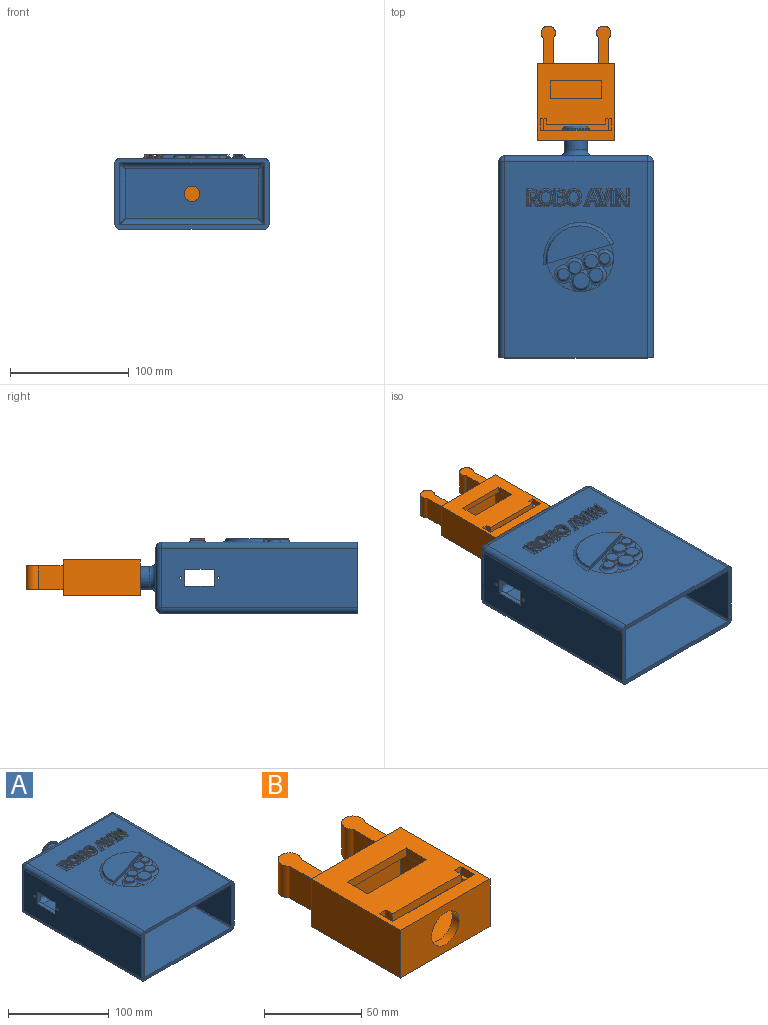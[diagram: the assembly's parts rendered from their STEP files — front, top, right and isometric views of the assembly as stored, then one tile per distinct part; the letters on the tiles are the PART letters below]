
ASSEMBLY  parts=2 mates=1
PART A: 289 faces, bbox 130.2x195.2x65.3 mm
  f0: cylinder r=6.5mm len=29mm, axis (0,-1,0), area 1144.2mm2, adj f1,f21,f22,f283,f284,f285,f286,f287
  f1: plane 18.89x8.5mm, normal (0,1,0), area 69.4mm2, adj f0,f4,f285,f288
  f2: cylinder r=11.5mm len=22.91mm, axis (0,1,0), area 34.1mm2, adj f3,f4,f285,f288
  f3: plane 22.91x10.5mm, normal (0,-1,0), area 62mm2, adj f2,f5,f285,f288
  f4: cone r=9.5mm half-angle=45deg, axis (0,-1,0), area 87.6mm2, adj f1,f2,f285,f288
  f5: cylinder r=9.5mm len=19mm, axis (0,-1,0), area 986.7mm2, adj f3,f59,f281,f283,f284,f285,f286,f287
  f6: plane 2.17x1.68mm, normal (0,0,1), area 1mm2, adj f274,f276,f277,f278
  f7: plane 18.13x9.48mm, normal (0,0,1), area 45.3mm2, adj f192,f273,f274
  f8: plane 13.06x6.59mm, normal (0,0,1), area 20.2mm2, adj f192,f274,f277
  f9: plane 0.13x0.05mm, normal (0,0,1), area 0mm2, adj f231,f234,f235
  f10: plane 3.32x1.5mm, normal (0,0,1), area 1.3mm2, adj f214,f215,f217
  f11: plane 165x120mm, normal (0,0,1), area 16089.2mm2, adj f14,f19,f20,f50,f60,f174,f179,f180
  f12: plane 120x50mm, normal (0,1,0), area 5339.5mm2, adj f43,f46,f47,f50,f59
  f13: plane 165x50mm, normal (-1,0,0), area 7892.4mm2, adj f14,f17,f19,f37,f38,f39,f40,f41
  f14: plane 130x60mm, normal (0,-1,0), area 1435.4mm2, adj f11,f13,f15,f16,f17,f18,f19,f20
  f15: plane 165x50mm, normal (1,0,0), area 7892.4mm2, adj f14,f18,f20,f31,f32,f33,f34,f35
  f16: plane 165x120mm, normal (0,0,-1), area 19800mm2, adj f14,f17,f18,f43
  f17: cylinder r=5mm len=165mm, axis (0,-1,0), area 1295.9mm2, adj f13,f14,f16,f44
  f18: cylinder r=5mm len=165mm, axis (0,1,0), area 1295.9mm2, adj f14,f15,f16,f45
  f19: cylinder r=5mm len=165mm, axis (0,1,0), area 1295.9mm2, adj f11,f13,f14,f48
  f20: cylinder r=5mm len=165mm, axis (0,-1,0), area 1295.9mm2, adj f11,f14,f15,f49
  f21: plane 18.89x8.5mm, normal (0,1,0), area 69.4mm2, adj f0,f282,f284,f287
  f22: plane 112x42mm, normal (0,-1,0), area 4571.3mm2, adj f0,f51,f54,f55,f58
  f23: plane 161x50mm, normal (1,0,0), area 7692.4mm2, adj f14,f27,f29,f37,f38,f39,f40,f41
  f24: plane 161x50mm, normal (-1,0,0), area 7692.4mm2, adj f14,f28,f30,f31,f32,f33,f34,f35
  f25: plane 161x120mm, normal (0,0,-1), area 19320mm2, adj f14,f29,f30,f51
  f26: plane 161x120mm, normal (0,0,1), area 19320mm2, adj f14,f27,f28,f58
  f27: cylinder r=1mm len=161mm, axis (0,-1,0), area 252.9mm2, adj f14,f23,f26,f56
  f28: cylinder r=1mm len=161mm, axis (0,1,0), area 252.9mm2, adj f14,f24,f26,f57
  f29: cylinder r=1mm len=161mm, axis (0,1,0), area 252.9mm2, adj f14,f23,f25,f52
  f30: cylinder r=1mm len=161mm, axis (0,-1,0), area 252.9mm2, adj f14,f24,f25,f53
  f31: plane 25x4mm, normal (0,0,1), area 100mm2, adj f15,f24,f32,f34
  f32: plane 14x4mm, normal (0,-1,0), area 56mm2, adj f15,f24,f31,f33
  f33: plane 25x4mm, normal (0,0,-1), area 100mm2, adj f15,f24,f32,f34
  f34: plane 14x4mm, normal (0,1,0), area 56mm2, adj f15,f24,f31,f33
  f35: cylinder r=1.1mm len=4mm, axis (-1,0,0), area 27.6mm2, adj f15,f24
  f36: cylinder r=1.1mm len=4mm, axis (-1,0,0), area 27.6mm2, adj f15,f24
  f37: plane 14x4mm, normal (0,1,0), area 56mm2, adj f13,f23,f38,f40
  f38: plane 25x4mm, normal (0,0,-1), area 100mm2, adj f13,f23,f37,f39
  f39: plane 14x4mm, normal (0,-1,0), area 56mm2, adj f13,f23,f38,f40
  f40: plane 25x4mm, normal (0,0,1), area 100mm2, adj f13,f23,f37,f39
  f41: cylinder r=1.1mm len=4mm, axis (-1,0,0), area 27.6mm2, adj f13,f23
  f42: cylinder r=1.1mm len=4mm, axis (-1,0,0), area 27.6mm2, adj f13,f23
  f43: cylinder r=5mm len=120mm, axis (-1,0,0), area 942.5mm2, adj f12,f16,f44,f45
  f44: sphere r=5mm, area 39.3mm2, adj f17,f43,f46
  f45: sphere r=5mm, area 53.5mm2, adj f18,f43,f47
  f46: cylinder r=5mm len=50mm, axis (0,0,1), area 392.7mm2, adj f12,f13,f44,f48
  f47: cylinder r=5mm len=50mm, axis (0,0,-1), area 392.7mm2, adj f12,f15,f45,f49
  f48: sphere r=5mm, area 39.3mm2, adj f19,f46,f50
  f49: sphere r=5mm, area 25mm2, adj f20,f47,f50
  f50: cylinder r=5mm len=120mm, axis (1,0,0), area 942.5mm2, adj f11,f12,f48,f49
  f51: cylinder r=5mm len=120mm, axis (-1,0,0), area 911.1mm2, adj f22,f25,f52,f53
  f52: bspline ~5.78x5mm, area 5.4mm2, adj f29,f51,f54
  f53: bspline ~5.78x5mm, area 5.4mm2, adj f30,f51,f55
  f54: cylinder r=5mm len=50mm, axis (0,0,-1), area 361.3mm2, adj f22,f23,f52,f56
  f55: cylinder r=5mm len=50mm, axis (0,0,1), area 361.3mm2, adj f22,f24,f53,f57
  f56: bspline ~5.78x5mm, area 5.4mm2, adj f27,f54,f58
  f57: bspline ~5.78x5mm, area 5.4mm2, adj f28,f55,f58
  f58: cylinder r=5mm len=120mm, axis (1,0,0), area 911.1mm2, adj f22,f26,f56,f57
  f59: torus R=14.5mm, axis (0,1,0), area 558.5mm2, adj f5,f12
  f60: plane 59.16x17.8mm, normal (0.29,-0.96,0), area 225.9mm2, adj f11,f61,f192,f193,f279
  f61: plane 53.39x31.67mm, normal (0,0,1), area 985.1mm2, adj f60,f279
  f62: plane 3x1.85mm, normal (0,1,0), area 5.6mm2, adj f63,f79,f80,f81
  f63: plane 4.44x3mm, normal (1,0,0), area 13.3mm2, adj f62,f64,f80,f81
  f64: plane 3x1.76mm, normal (0,-1,0), area 5.3mm2, adj f63,f65,f80,f81
  f65: extruded ~3x2.18mm, area 6.8mm2, adj f64,f66,f80,f81
  f66: extruded ~3x1.66mm, area 5.6mm2, adj f65,f67,f80,f81
  f67: extruded ~3x1.71mm, area 5.7mm2, adj f66,f79,f80,f81
  f68: plane 4.83x1.5mm, normal (1,0,0), area 7.2mm2, adj f69,f78,f80,f206
  f69: plane 2.43x1.5mm, normal (0,-1,0), area 3.6mm2, adj f68,f70,f80,f208
  f70: plane 4.83x2.81mm, normal (-0.86,-0.5,0), area 8.4mm2, adj f69,f71,f80,f210
  f71: plane 1.6x1.5mm, normal (0,-1,0), area 2.4mm2, adj f70,f72,f80,f212
  f72: plane 5.22x3.16mm, normal (0.86,0.52,0), area 9.1mm2, adj f71,f73,f80,f214
  f73: extruded ~3.12x2.34mm, area 6.3mm2, adj f72,f74,f80,f215
  f74: extruded ~2.46x1.5mm, area 4.1mm2, adj f73,f75,f80,f216
  f75: extruded ~3.16x1.5mm, area 5mm2, adj f74,f76,f80,f213
  f76: plane 3.19x1.5mm, normal (0,1,0), area 4.8mm2, adj f75,f77,f80,f211
  f77: plane 11.62x1.5mm, normal (-1,0,0), area 17.4mm2, adj f76,f78,f80,f209
  f78: plane 1.5x1.35mm, normal (0,-1,0), area 2mm2, adj f68,f77,f80,f207
  f79: extruded ~3x2.1mm, area 6.6mm2, adj f62,f67,f80,f81
  f80: plane 11.62x8.19mm, normal (0,0,1), area 40.5mm2, adj f62,f63,f64,f65,f66,f67,f68,f69
  f81: plane 4.62x4.44mm, normal (0,0,1), area 18.5mm2, adj f62,f63,f64,f65,f66,f67,f79
  f82: extruded ~3.58x3mm, area 11.4mm2, adj f83,f97,f98,f99
  f83: extruded ~3.55x3mm, area 11.3mm2, adj f82,f84,f98,f99
  f84: extruded ~3x2.94mm, area 9.9mm2, adj f83,f85,f98,f99
  f85: extruded ~3x2.9mm, area 9.8mm2, adj f84,f86,f98,f99
  f86: extruded ~3.56x3mm, area 11.3mm2, adj f85,f87,f98,f99
  f87: extruded ~3.59x3mm, area 11.4mm2, adj f86,f88,f98,f99
  f88: extruded ~3x2.92mm, area 9.8mm2, adj f87,f97,f98,f99
  f89: extruded ~4.39x1.5mm, area 7.1mm2, adj f90,f96,f98,f223
  f90: extruded ~4.39x1.5mm, area 7.1mm2, adj f89,f91,f98,f224
  f91: extruded ~3.91x1.59mm, area 6.5mm2, adj f90,f92,f98,f222
  f92: extruded ~3.97x1.56mm, area 6.6mm2, adj f91,f93,f98,f220
  f93: extruded ~4.4x1.5mm, area 7.1mm2, adj f92,f94,f98,f218
  f94: extruded ~4.43x1.5mm, area 7.1mm2, adj f93,f95,f98,f217
  f95: extruded ~3.96x1.57mm, area 6.6mm2, adj f94,f96,f98,f219
  f96: extruded ~3.92x1.6mm, area 6.6mm2, adj f89,f95,f98,f221
  f97: extruded ~3x2.92mm, area 9.8mm2, adj f82,f88,f98,f99
  f98: plane 11.96x10.69mm, normal (0,0,1), area 42.7mm2, adj f82,f83,f84,f85,f86,f87,f88,f89
  f99: plane 9.57x7.83mm, normal (0,0,1), area 62.1mm2, adj f82,f83,f84,f85,f86,f87,f88,f97
  f100: plane 4.35x3mm, normal (1,0,0), area 13mm2, adj f101,f124,f125,f126
  f101: plane 3x2.31mm, normal (0,-1,0), area 6.9mm2, adj f100,f102,f125,f126
  f102: extruded ~3x2.21mm, area 6.9mm2, adj f101,f103,f125,f126
  f103: extruded ~3x1.59mm, area 5.5mm2, adj f102,f104,f125,f126
  f104: extruded ~3x1.71mm, area 5.8mm2, adj f103,f105,f125,f126
  f105: extruded ~3x2.12mm, area 6.7mm2, adj f104,f124,f125,f126
  f106: plane 3x2.23mm, normal (0,1,0), area 6.7mm2, adj f107,f122,f125,f127
  f107: plane 3.8x3mm, normal (1,0,0), area 11.4mm2, adj f106,f108,f125,f127
  f108: plane 3x1.99mm, normal (0,-1,0), area 6mm2, adj f107,f109,f125,f127
  f109: extruded ~3x2.23mm, area 6.9mm2, adj f108,f110,f125,f127
  f110: extruded ~3x1.41mm, area 5mm2, adj f109,f111,f125,f127
  f111: extruded ~3x1.51mm, area 5.1mm2, adj f110,f122,f125,f127
  f112: plane 3.28x1.5mm, normal (0,1,0), area 4.9mm2, adj f113,f123,f125,f226
  f113: plane 11.62x1.5mm, normal (-1,0,0), area 17.4mm2, adj f112,f114,f125,f225
  f114: plane 4.05x1.5mm, normal (0,-1,0), area 6.1mm2, adj f113,f115,f125,f227
  f115: extruded ~2.94x1.5mm, area 4.7mm2, adj f114,f116,f125,f229
  f116: extruded ~2.43x1.5mm, area 4.1mm2, adj f115,f117,f125,f233
  f117: extruded ~2.78x2.65mm, area 6.4mm2, adj f116,f118,f125,f234
  f118: plane 1.85x0.09mm, normal (1,0,0), area 0.1mm2, adj f117,f119,f125,f230,f234
  f119: extruded ~1.68x1.5mm, area 2.9mm2, adj f118,f120,f125,f230
  f120: extruded ~1.71x1.5mm, area 2.8mm2, adj f119,f121,f125,f231
  f121: extruded ~2.18x1.5mm, area 3.8mm2, adj f120,f123,f125,f232
  f122: extruded ~3x2.06mm, area 6.4mm2, adj f106,f111,f125,f127
  f123: extruded ~3.35x1.5mm, area 5.2mm2, adj f112,f121,f125,f228
  f124: plane 3x2.43mm, normal (0,1,0), area 7.3mm2, adj f100,f105,f125,f126
  f125: plane 11.62x8.05mm, normal (0,0,1), area 46mm2, adj f100,f101,f102,f103,f104,f105,f106,f107
  f126: plane 5.25x4.35mm, normal (0,0,1), area 20.8mm2, adj f100,f101,f102,f103,f104,f105,f124
  f127: plane 4.91x3.8mm, normal (0,0,1), area 17.1mm2, adj f106,f107,f108,f109,f110,f111,f122
  f128: extruded ~3.58x3mm, area 11.4mm2, adj f129,f143,f144,f145
  f129: extruded ~3.55x3mm, area 11.3mm2, adj f128,f130,f144,f145
  f130: extruded ~3x2.94mm, area 9.9mm2, adj f129,f131,f144,f145
  f131: extruded ~3x2.9mm, area 9.8mm2, adj f130,f132,f144,f145
  f132: extruded ~3.56x3mm, area 11.3mm2, adj f131,f133,f144,f145
  f133: extruded ~3.59x3mm, area 11.4mm2, adj f132,f134,f144,f145
  f134: extruded ~3x2.92mm, area 9.8mm2, adj f133,f143,f144,f145
  f135: extruded ~4.39x1.5mm, area 7.1mm2, adj f136,f142,f144,f242
  f136: extruded ~4.39x1.5mm, area 7.1mm2, adj f135,f137,f144,f240
  f137: extruded ~3.91x1.59mm, area 6.5mm2, adj f136,f138,f144,f238
  f138: extruded ~3.97x1.56mm, area 6.6mm2, adj f137,f139,f144,f236
  f139: extruded ~4.4x1.5mm, area 7.1mm2, adj f138,f140,f144,f235
  f140: extruded ~4.43x1.5mm, area 7.1mm2, adj f139,f141,f144,f237
  f141: extruded ~3.96x1.57mm, area 6.6mm2, adj f140,f142,f144,f239
  f142: extruded ~3.92x1.6mm, area 6.6mm2, adj f135,f141,f144,f241
  f143: extruded ~3x2.92mm, area 9.8mm2, adj f128,f134,f144,f145
  f144: plane 11.96x10.69mm, normal (0,0,1), area 42.7mm2, adj f128,f129,f130,f131,f132,f133,f134,f135
  f145: plane 9.57x7.83mm, normal (0,0,1), area 62.1mm2, adj f128,f129,f130,f131,f132,f133,f134,f143
  f146: plane 3.6x3mm, normal (-0.94,-0.35,0), area 11.5mm2, adj f147,f158,f159,f160
  f147: plane 3.76x3mm, normal (0,1,0), area 11.3mm2, adj f146,f148,f159,f160
  f148: plane 3.6x3mm, normal (0.94,-0.35,0), area 11.6mm2, adj f147,f149,f159,f160
  f149: extruded ~3x1.68mm, area 5.2mm2, adj f148,f158,f159,f160
  f150: plane 3.69x1.5mm, normal (-0.93,-0.36,0), area 6mm2, adj f151,f157,f159,f258
  f151: plane 1.5x1.4mm, normal (0,-1,0), area 2.1mm2, adj f150,f152,f159,f259
  f152: plane 11.67x4.57mm, normal (0.93,0.36,0), area 18.8mm2, adj f151,f153,f159,f257
  f153: plane 1.5x1.14mm, normal (0,1,0), area 1.7mm2, adj f152,f154,f159,f255
  f154: plane 11.67x4.59mm, normal (-0.93,0.37,0), area 18.8mm2, adj f153,f155,f159,f253
  f155: plane 1.5x1.37mm, normal (0,-1,0), area 2.1mm2, adj f154,f156,f159,f252
  f156: plane 3.69x1.5mm, normal (0.93,-0.36,0), area 5.9mm2, adj f155,f157,f159,f254
  f157: plane 4.66x1.5mm, normal (0,-1,0), area 7mm2, adj f150,f156,f159,f256
  f158: extruded ~3x1.68mm, area 5.3mm2, adj f146,f149,f159,f160
  f159: plane 11.67x10.3mm, normal (0,0,1), area 34.7mm2, adj f146,f147,f148,f149,f150,f151,f152,f153
  f160: plane 5.28x3.76mm, normal (0,0,1), area 9.5mm2, adj f146,f147,f148,f149,f158
  f161: plane 1.5x1.45mm, normal (0,1,0), area 2.2mm2, adj f162,f169,f170,f246
  f162: plane 7.47x2.65mm, normal (-0.94,0.33,0), area 11.9mm2, adj f161,f163,f170,f248
  f163: extruded ~2.57x1.5mm, area 4mm2, adj f162,f164,f170,f250
  f164: extruded ~2.52x1.5mm, area 3.9mm2, adj f163,f165,f170,f251
  f165: plane 7.52x2.67mm, normal (0.94,0.33,0), area 12mm2, adj f164,f166,f170,f249
  f166: plane 1.5x1.43mm, normal (0,1,0), area 2.1mm2, adj f165,f167,f170,f247
  f167: plane 11.62x4.17mm, normal (-0.94,-0.34,0), area 18.5mm2, adj f166,f168,f170,f245
  f168: plane 1.5x1.34mm, normal (0,-1,0), area 2mm2, adj f167,f169,f170,f243
  f169: plane 11.62x4.19mm, normal (0.94,-0.34,0), area 18.5mm2, adj f161,f168,f170,f244
  f170: plane 11.62x9.69mm, normal (0,0,1), area 31.3mm2, adj f161,f162,f163,f164,f165,f166,f167,f168
  f171: plane 11.62x1.5mm, normal (-1,0,0), area 17.4mm2, adj f172,f174,f175,f271
  f172: plane 1.5x1.35mm, normal (0,-1,0), area 2mm2, adj f171,f173,f175,f272
  f173: plane 11.62x1.5mm, normal (1,0,0), area 17.4mm2, adj f172,f174,f175,f270
  f174: plane 3.63x3.01mm, normal (0,1,0), area 4.9mm2, adj f11,f171,f173,f175,f244,f270,f271
  f175: plane 11.62x1.35mm, normal (0,0,1), area 15.7mm2, adj f171,f172,f173,f174
  f176: plane 1.54x1.5mm, normal (0,-1,0), area 2.3mm2, adj f177,f190,f191,f265
  f177: plane 11.62x1.5mm, normal (1,0,0), area 17.4mm2, adj f176,f178,f191,f263
  f178: plane 1.5x1.26mm, normal (0,1,0), area 1.9mm2, adj f177,f179,f191,f261
  f179: plane 8.17x3mm, normal (-1,0,0), area 20.5mm2, adj f11,f178,f180,f191,f261
  f180: extruded ~3x1.67mm, area 4.9mm2, adj f11,f179,f181,f191,f260
  f181: extruded ~2.8x1.38mm, area 3.4mm2, adj f180,f182,f191,f260
  f182: plane 1.91x0.08mm, normal (0,1,0), area 0.1mm2, adj f181,f183,f191,f260
  f183: plane 9.71x6.33mm, normal (0.84,0.55,0), area 17.4mm2, adj f182,f184,f191,f260
  f184: plane 1.53x1.5mm, normal (0,1,0), area 2.3mm2, adj f183,f185,f191,f262
  f185: plane 11.62x1.5mm, normal (-1,0,0), area 17.4mm2, adj f184,f186,f191,f264
  f186: plane 1.5x1.25mm, normal (0,-1,0), area 1.9mm2, adj f185,f187,f191,f266
  f187: plane 6.6x1.5mm, normal (1,0,0), area 9.9mm2, adj f186,f188,f191,f268
  f188: extruded ~3.15x1.5mm, area 4.7mm2, adj f187,f189,f191,f269
  f189: plane 1.8x0.07mm, normal (0,-1,0), area 0.1mm2, adj f188,f190,f191,f267,f269
  f190: plane 9.75x6.35mm, normal (-0.84,-0.55,0), area 17.5mm2, adj f176,f189,f191,f267
  f191: plane 11.62x9.08mm, normal (0,0,1), area 44.6mm2, adj f176,f177,f178,f179,f180,f181,f182,f183
  f192: cylinder r=27.99mm len=55.64mm, axis (0,0,1), area 95.4mm2, adj f7,f8,f11,f60,f193,f273,f274,f277
  f193: plane 55.58x39.34mm, normal (0,0,1), area 263.7mm2, adj f60,f192,f273,f275,f276,f277,f278
  f194: plane 13.52x13.52mm, normal (0,0,1), area 143.5mm2, adj f195
  f195: cylinder r=6.76mm len=13.52mm, axis (0,0,-1), area 42.5mm2, adj f194,f277
  f196: plane 8.85x8.85mm, normal (0,0,1), area 61.5mm2, adj f197
  f197: cylinder r=4.42mm len=8.85mm, axis (0,0,-1), area 27.8mm2, adj f196,f273
  f198: plane 11.17x11.17mm, normal (0,0,1), area 98.1mm2, adj f199
  f199: cylinder r=5.59mm len=11.17mm, axis (0,0,-1), area 35.1mm2, adj f198,f276
  f200: plane 10.12x10.12mm, normal (0,0,1), area 80.4mm2, adj f201
  f201: cylinder r=5.06mm len=10.12mm, axis (0,0,-1), area 31.8mm2, adj f200,f278
  f202: plane 9.55x9.55mm, normal (0,0,1), area 71.7mm2, adj f203
  f203: cylinder r=4.78mm len=9.55mm, axis (0,0,-1), area 30mm2, adj f202,f275
  f204: plane 11.31x11.31mm, normal (0,0,1), area 100.4mm2, adj f205
  f205: cylinder r=5.65mm len=11.31mm, axis (0,0,-1), area 35.5mm2, adj f204,f274
  f206: cylinder r=1.5mm len=6.33mm, axis (0,1,0), area 11.4mm2, adj f11,f68,f207,f208
  f207: cylinder r=1.5mm len=4.35mm, axis (1,0,0), area 6.7mm2, adj f11,f78,f206,f209
  f208: cylinder r=1.5mm len=2.43mm, axis (1,0,0), area 3.7mm2, adj f11,f69,f206,f210
  f209: cylinder r=1.5mm len=14.62mm, axis (0,-1,0), area 30.9mm2, adj f11,f77,f207,f211
  f210: cylinder r=1.5mm len=6.33mm, axis (0.5,-0.86,0), area 13.2mm2, adj f11,f70,f208,f212
  f211: cylinder r=1.5mm len=4.69mm, axis (-1,0,0), area 9.3mm2, adj f11,f76,f209,f213
  f212: cylinder r=1.5mm len=5.12mm, axis (1,0,0), area 7.9mm2, adj f11,f71,f210,f214
  f213: bspline ~5.7x2.68mm, area 8.7mm2, adj f11,f75,f211,f216
  f214: cylinder r=1.5mm len=8.27mm, axis (-0.52,0.86,0), area 15.6mm2, adj f10,f11,f72,f212,f215,f217
  f215: bspline ~5.23x4.94mm, area 9.3mm2, adj f10,f73,f214,f216,f217,f218
  f216: bspline ~4.76x3.06mm, area 7.5mm2, adj f11,f74,f213,f215,f218
  f217: bspline ~7.62x3.42mm, area 12.1mm2, adj f10,f11,f94,f214,f215,f218,f219
  f218: bspline ~7.55x3.42mm, area 11.3mm2, adj f11,f93,f215,f216,f217,f220
  f219: bspline ~6.91x3.89mm, area 11.4mm2, adj f11,f95,f217,f221
  f220: bspline ~6.94x3.89mm, area 11.5mm2, adj f11,f92,f218,f222
  f221: bspline ~6.84x3.91mm, area 11.4mm2, adj f11,f96,f219,f223
  f222: bspline ~6.02x3.89mm, area 11.4mm2, adj f11,f91,f220,f224
  f223: bspline ~7.54x3.43mm, area 11.7mm2, adj f11,f89,f221,f224,f225
  f224: bspline ~7.54x3.43mm, area 11.7mm2, adj f11,f90,f222,f223,f225
  f225: cylinder r=1.5mm len=14.62mm, axis (0,-1,0), area 30.3mm2, adj f11,f113,f223,f224,f226,f227
  f226: cylinder r=1.5mm len=4.78mm, axis (-1,0,0), area 9.5mm2, adj f11,f112,f225,f228
  f227: cylinder r=1.5mm len=5.55mm, axis (1,0,0), area 11.3mm2, adj f11,f114,f225,f229
  f228: bspline ~5.62x2.63mm, area 8.9mm2, adj f11,f123,f226,f232
  f229: bspline ~4.68x2.86mm, area 8.3mm2, adj f11,f115,f227,f233
  f230: bspline ~3.37x2.49mm, area 2.5mm2, adj f118,f119,f231,f234
  f231: bspline ~3.66x2.44mm, area 4.8mm2, adj f9,f120,f230,f232,f234,f235
  f232: bspline ~4.47x3.09mm, area 7.2mm2, adj f11,f121,f228,f231,f235
  f233: bspline ~4.27x3.15mm, area 7.3mm2, adj f11,f116,f229,f234,f237
  f234: bspline ~5.46x4.31mm, area 7.7mm2, adj f9,f117,f118,f230,f231,f233,f235,f237
  f235: bspline ~7.55x3.42mm, area 11.6mm2, adj f9,f11,f139,f231,f232,f234,f236,f237
  f236: bspline ~6.94x3.89mm, area 11.5mm2, adj f11,f138,f235,f238
  f237: bspline ~7.62x3.42mm, area 11.1mm2, adj f11,f140,f233,f234,f235,f239
  f238: bspline ~6.02x3.89mm, area 11.4mm2, adj f11,f137,f236,f240
  f239: bspline ~6.91x3.89mm, area 11.4mm2, adj f11,f141,f237,f241
  f240: bspline ~7.54x3.43mm, area 12mm2, adj f11,f136,f238,f242
  f241: bspline ~6.84x3.91mm, area 11.4mm2, adj f11,f142,f239,f242
  f242: bspline ~7.54x3.43mm, area 12mm2, adj f11,f135,f240,f241
  f243: cylinder r=1.5mm len=3.44mm, axis (1,0,0), area 5.6mm2, adj f11,f168,f244,f245
  f244: cylinder r=1.5mm len=15.13mm, axis (0.34,0.94,0), area 30.5mm2, adj f11,f169,f174,f243,f246,f271
  f245: cylinder r=1.5mm len=15.12mm, axis (0.34,-0.94,0), area 32.8mm2, adj f11,f167,f243,f247
  f246: cylinder r=1.5mm len=4.65mm, axis (-1,0,0), area 7.2mm2, adj f11,f161,f244,f248
  f247: cylinder r=1.5mm len=4.62mm, axis (-1,0,0), area 7.1mm2, adj f11,f166,f245,f249
  f248: cylinder r=1.5mm len=8.97mm, axis (-0.33,-0.94,0), area 19.2mm2, adj f11,f162,f246,f249,f250
  f249: cylinder r=1.5mm len=9.02mm, axis (-0.33,0.94,0), area 18.9mm2, adj f11,f165,f247,f248,f250,f251
  f250: bspline ~4.16x2.53mm, area 2.7mm2, adj f163,f248,f249,f251
  f251: bspline ~3.78x2.38mm, area 2.1mm2, adj f164,f249,f250
  f252: cylinder r=1.5mm len=4.6mm, axis (1,0,0), area 7mm2, adj f11,f155,f253,f254
  f253: cylinder r=1.5mm len=15.22mm, axis (-0.37,-0.93,0), area 33.3mm2, adj f11,f154,f252,f255
  f254: cylinder r=1.5mm len=5.19mm, axis (0.36,0.93,0), area 9.3mm2, adj f11,f156,f252,f256
  f255: cylinder r=1.5mm len=3.18mm, axis (-1,0,0), area 5.1mm2, adj f11,f153,f253,f257
  f256: cylinder r=1.5mm len=4.66mm, axis (1,0,0), area 8.6mm2, adj f11,f157,f254,f258
  f257: cylinder r=1.5mm len=15.21mm, axis (-0.36,0.93,0), area 33.3mm2, adj f11,f152,f255,f259
  f258: cylinder r=1.5mm len=5.19mm, axis (0.36,-0.93,0), area 9.3mm2, adj f11,f150,f256,f259
  f259: cylinder r=1.5mm len=4.62mm, axis (1,0,0), area 7.1mm2, adj f11,f151,f257,f258
  f260: cylinder r=1.5mm len=11.24mm, axis (-0.55,0.84,0), area 26.2mm2, adj f11,f180,f181,f182,f183,f262
  f261: cylinder r=1.5mm len=2.76mm, axis (-1,0,0), area 4.7mm2, adj f11,f178,f179,f263
  f262: cylinder r=1.5mm len=3.84mm, axis (-1,0,0), area 6.3mm2, adj f11,f184,f260,f264
  f263: cylinder r=1.5mm len=14.62mm, axis (0,1,0), area 30.9mm2, adj f11,f177,f261,f265
  f264: cylinder r=1.5mm len=14.62mm, axis (0,-1,0), area 30.9mm2, adj f11,f185,f262,f266
  f265: cylinder r=1.5mm len=3.85mm, axis (1,0,0), area 6.4mm2, adj f11,f176,f263,f267
  f266: cylinder r=1.5mm len=4.25mm, axis (1,0,0), area 6.5mm2, adj f11,f186,f264,f268
  f267: cylinder r=1.5mm len=11.26mm, axis (0.55,-0.84,0), area 23.7mm2, adj f11,f189,f190,f265,f268,f269
  f268: cylinder r=1.5mm len=8.1mm, axis (0,1,0), area 16.7mm2, adj f11,f187,f266,f267,f269
  f269: bspline ~4.34x1.69mm, area 3.6mm2, adj f188,f189,f267,f268
  f270: cylinder r=1.5mm len=13.12mm, axis (0,1,0), area 29.1mm2, adj f11,f173,f174,f272
  f271: cylinder r=1.5mm len=13.12mm, axis (0,-1,0), area 27.6mm2, adj f11,f171,f174,f244,f272
  f272: cylinder r=1.5mm len=4.35mm, axis (1,0,0), area 6.7mm2, adj f11,f172,f270,f271
  f273: torus R=7.42mm, axis (0,0,1), area 144mm2, adj f7,f192,f193,f197,f274,f276
  f274: torus R=8.65mm, axis (0,0,1), area 152.1mm2, adj f6,f7,f8,f192,f205,f273,f276,f277
  f275: torus R=7.78mm, axis (0,0,1), area 149.8mm2, adj f193,f203,f277,f278
  f276: torus R=8.59mm, axis (0,0,1), area 151.5mm2, adj f6,f193,f199,f273,f274,f278
  f277: torus R=9.76mm, axis (0,0,1), area 175.3mm2, adj f6,f8,f192,f193,f195,f274,f275,f278
  f278: torus R=8.06mm, axis (0,0,1), area 129.9mm2, adj f6,f193,f201,f275,f276,f277
  f279: torus R=31.12mm, axis (0,0,1), area 389.5mm2, adj f11,f60,f61
  f280: cylinder r=11.5mm len=22.91mm, axis (0,1,0), area 34.1mm2, adj f281,f282,f284,f287
  f281: plane 22.91x10.5mm, normal (0,-1,0), area 62mm2, adj f5,f280,f284,f287
  f282: cone r=9.5mm half-angle=45deg, axis (0,-1,0), area 87.6mm2, adj f21,f280,f284,f287
  f283: plane 3.08x2mm, normal (0,1,0), area 6mm2, adj f0,f5,f284,f285
  f284: plane 10.02x5.05mm, normal (0,0,1), area 34.3mm2, adj f0,f5,f21,f280,f281,f282,f283
  f285: plane 10.02x5.05mm, normal (0,0,-1), area 34.3mm2, adj f0,f1,f2,f3,f4,f5,f283
  f286: plane 3.08x2mm, normal (0,1,0), area 6mm2, adj f0,f5,f287,f288
  f287: plane 10.02x5.05mm, normal (0,0,1), area 34.3mm2, adj f0,f5,f21,f280,f281,f282,f286
  f288: plane 10.02x5.05mm, normal (0,0,-1), area 34.3mm2, adj f0,f1,f2,f3,f4,f5,f286
PART B: 39 faces, bbox 65x96.2x30 mm
  f0: plane 27.5x20mm, normal (0,1,0), area 392.9mm2, adj f31,f33,f34,f38
  f1: plane 9.75x2.16mm, normal (0,0,1), area 21.1mm2, adj f7,f13,f18,f35
  f2: plane 65x30mm, normal (0,1,0), area 1614.5mm2, adj f3,f5,f6,f19,f21,f22,f24,f25
  f3: plane 65x30mm, normal (-1,0,0), area 1950mm2, adj f2,f4,f6,f19
  f4: plane 65x30mm, normal (0,-1,0), area 1635.8mm2, adj f3,f5,f6,f19,f38
  f5: plane 65x30mm, normal (1,0,0), area 1950mm2, adj f2,f4,f6,f19
  f6: plane 65x65mm, normal (0,0,-1), area 4225mm2, adj f2,f3,f4,f5
  f7: plane 59.33x5mm, normal (0,1,0), area 296.6mm2, adj f1,f8,f18,f19,f20,f31
  f8: plane 9.75x5mm, normal (1,0,0), area 48.7mm2, adj f7,f9,f19,f20
  f9: plane 5x4.66mm, normal (0,-1,0), area 23.3mm2, adj f8,f10,f19,f20,f32
  f10: plane 5x4.75mm, normal (-1,0,0), area 23.7mm2, adj f9,f11,f19,f32
  f11: plane 50x5mm, normal (0,-1,0), area 250mm2, adj f10,f12,f19,f32
  f12: plane 5x4.75mm, normal (1,0,0), area 23.7mm2, adj f11,f13,f19,f32
  f13: plane 5x4.66mm, normal (0,-1,0), area 23.3mm2, adj f1,f12,f18,f19,f32
  f14: plane 15x5mm, normal (1,0,0), area 75mm2, adj f15,f17,f19,f32
  f15: plane 43x5mm, normal (0,-1,0), area 215mm2, adj f14,f16,f19,f32
  f16: plane 15x5mm, normal (-1,0,0), area 75mm2, adj f15,f17,f19,f32
  f17: plane 43x5mm, normal (0,1,0), area 215mm2, adj f14,f16,f19,f32
  f18: plane 9.75x5mm, normal (-1,0,0), area 48.7mm2, adj f1,f7,f13,f19
  f19: plane 65x65mm, normal (0,0,1), area 3239.1mm2, adj f2,f3,f4,f5,f7,f8,f9,f10
  f20: plane 9.75x2.16mm, normal (0,0,1), area 21.1mm2, adj f7,f8,f9,f33
  f21: plane 20.94x20mm, normal (-1,0,0), area 418.8mm2, adj f2,f23,f24,f25
  f22: plane 20.94x20mm, normal (1,0,0), area 418.8mm2, adj f2,f23,f24,f25
  f23: cylinder r=5.98mm len=20mm, axis (0,0,1), area 564.9mm2, adj f21,f22,f24,f25
  f24: plane 31.17x11.95mm, normal (0,0,-1), area 277.9mm2, adj f2,f21,f22,f23
  f25: plane 31.17x11.95mm, normal (0,0,1), area 277.9mm2, adj f2,f21,f22,f23
  f26: plane 20.94x20mm, normal (-1,0,0), area 418.8mm2, adj f2,f28,f29,f30
  f27: plane 20.94x20mm, normal (1,0,0), area 418.8mm2, adj f2,f28,f29,f30
  f28: cylinder r=5.98mm len=20mm, axis (0,0,1), area 564.9mm2, adj f26,f27,f29,f30
  f29: plane 31.17x11.95mm, normal (0,0,-1), area 277.9mm2, adj f2,f26,f27,f28
  f30: plane 31.17x11.95mm, normal (0,0,1), area 277.9mm2, adj f2,f26,f27,f28
  f31: plane 55x3.54mm, normal (0,0,-1), area 194.5mm2, adj f0,f7,f33,f35,f37
  f32: plane 55x46.46mm, normal (0,0,-1), area 1886.7mm2, adj f9,f10,f11,f12,f13,f14,f15,f16
  f33: plane 55x20mm, normal (1,0,0), area 1100mm2, adj f0,f20,f31,f32,f34,f36
  f34: plane 55x55mm, normal (0,0,1), area 3025mm2, adj f0,f33,f35,f36,f37
  f35: plane 55x20mm, normal (-1,0,0), area 1100mm2, adj f1,f31,f32,f34,f36,f37
  f36: plane 55x20mm, normal (0,-1,0), area 1100mm2, adj f32,f33,f34,f35
  f37: plane 27.5x20mm, normal (0,1,0), area 392.9mm2, adj f31,f34,f35,f38
  f38: cylinder r=10mm len=20mm, axis (0,-1,0), area 314.2mm2, adj f0,f4,f37
PLACE A t=(21.92,-72.96,24.8)mm
PLACE B t=(82.67,66.49,64.8)mm
MATE revolute B.f38 <-> A.f0  axis (0,-1,0) through (5.39,76.77,54.8)mm
